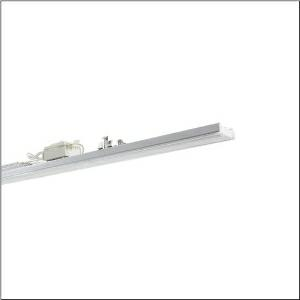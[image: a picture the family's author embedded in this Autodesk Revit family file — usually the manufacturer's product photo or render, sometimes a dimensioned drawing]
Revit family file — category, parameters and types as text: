
# Revit family: licross_r__11_recessed_mo_51tl18dv6e5g_8643
name_source: partatom
category: Lighting Fixtures
units: mm (PartAtom-declared; Revit-internal decimal feet)

## family parameters
Cut with Voids When Loaded = No
Host = Face
Light Source = No
Part Type = Normal
Room Calculation Point = No
Round Connector Dimension = Use Diameter
Shared = No

## types (1)
- --- (1 x LED, 14560 lm, 84.1 W, 6500K)
    Apparent Load = 84 VA
    CIE Flux Codes = 83 96 99 100 100
    Color Rendering = 80
    Color Temperature = 6500K
    Default Elevation = 1800 mm
    Description = Licross® 11 Recessed MO, luminaire insert, of sheet steel, coil coated, white, length: 2.250mm, width: 66mm, height: 67mm, LED rated luminous flux: 14.560lm, light colour: 865, control gear: DALI 2, with plug, 5-pole, with phase selection, mains connection: 220..240V, AC, 50/60Hz, rated input power: 84W, internal wiring halogen-free, primary light control with lens, of plastic, primary optical cover: cover, of PMMA, light emission: direct distribution, primary light characteristic: symmetric, protection rating (complete): IP40, insulation class (complete): insulation class I (protective earthing), certification: CE, ENEC, VDE, UKCA, protection symbol: D if used in an environment without relevant dust loads with corresponding accessories, impact resistance: IK06, permissible ambient temperature for indoor applications: -25..+35°C, corresponds to IFS (International Featured Standards) requirements for safety and quality in the food industry, reducing of maximum allowable ambient temperature of 5°C with ceiling mounting, LABS conformity tested according to VDMA 24364:2018-05, packaging unit: 1 piece
    Height = 58 mm
    Lamp = 1 x LED
    Lamp Light Flux = 14560 lm
    Lamp Power = 84.1 W
    Lamp count = 1
    Length = 2250 mm
    Luminous efficacy = 173 lm/W
    Manufacturer = Siteco
    ModVariant = No
    Model = 51TL18DV6E5G
    Mounting Place = Ceiling
    Mounting Type = Pendant
    Number of Poles = 1
    OnlyDefault = Yes
    Power Factor = 1
    Product Name = Licross® 11 Recessed MO
    Product group = luminaire insert | ceiling pendant
    ProductGroupID = 902
    Protection Class = Protection class I
    Protection Degree = IP 40
    RLX_Detail_Level = 1
    RLX_Emergency_Light_Flux = 0 lm
    RLX_Emergency_Type = 0
    RLX_Emergency_Type_DB = No
    RlxData = <blob elided: 29121 chars, md5=64abe1ad>
    Socket = socket
    Standby Power = 0 W
    System Light Flux = 14560 lm
    System Power = 84 W
    Type Comments = factory setting: luminous flux: 100 % | dim-lin: 254 | 378 mA
    Type Image = l_1296930.jpg
    URL = http://relux.com
    VarID = @adj_042573
    Voltage = 0 V
    Weight = 0.00 kg
    Width = 66 mm

## geometry (parser evidence)
native form markers: Blend x4, Sweep x9
no freeform markers — native parametric forms only
